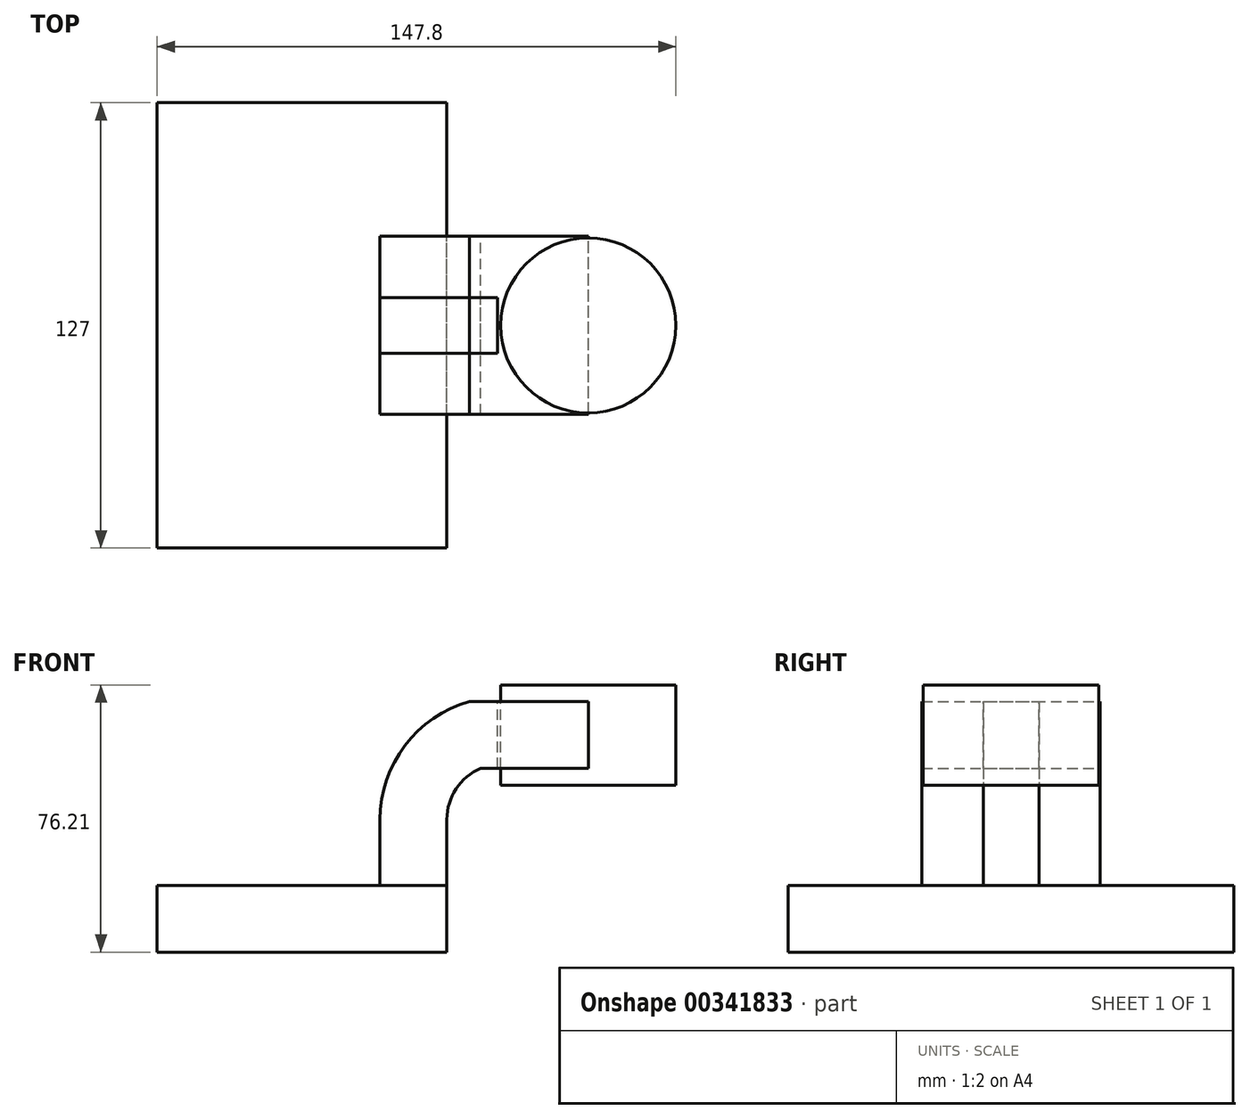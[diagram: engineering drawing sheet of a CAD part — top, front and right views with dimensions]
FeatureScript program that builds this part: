
annotation { "Feature Type Name" : "Feature", "Feature Type Description" : "" }
export const myFeature = defineFeature(function(context is Context, id is Id, definition is map)
    precondition{}
    {
        {
            var Q0;
            Q0=qCreatedBy(makeId("Front.planeOp"),FACE);
            var sketch = newSketch(context, id + "F0", { "sketchPlane" : qUnion([Q0])});
            skLineSegment(sketch, "E0.bottom", {"start": v(41.28, -9.52) * mm, "end": v(-41.28, -9.53) * mm});
            skLineSegment(sketch, "E0.top", {"start": v(41.28, 9.53) * mm, "end": v(-41.28, 9.53) * mm});
            skLineSegment(sketch, "E0.left", {"start": v(41.28, -9.52) * mm, "end": v(41.28, 9.53) * mm});
            skLineSegment(sketch, "E0.right", {"start": v(-41.28, -9.53) * mm, "end": v(-41.28, 9.53) * mm});
            skPoint(sketch, "E0.middle", {"position": v(0, 0) * mm});
            skLineSegment(sketch, "E1.bottom", {"start": v(106.53, 38.1) * mm, "end": v(55.73, 38.1) * mm});
            skLineSegment(sketch, "E1.top", {"start": v(106.53, 66.68) * mm, "end": v(55.73, 66.68) * mm});
            skLineSegment(sketch, "E1.left", {"start": v(106.53, 38.1) * mm, "end": v(106.53, 66.68) * mm});
            skLineSegment(sketch, "E1.right", {"start": v(55.73, 38.1) * mm, "end": v(55.73, 66.68) * mm});
            skPoint(sketch, "E1.middle", {"position": v(81.13, 52.39) * mm});
            skLineSegment(sketch, "E2", {"start": v(41.28, 9.53) * mm, "end": v(41.28, 28.3) * mm});
            skArc(sketch, "E3", {"start": v(41.27, 28.3) * mm, "mid": v(43.9, 37.02) * mm, "end": v(50.88, 42.88) * mm});
            skLineSegment(sketch, "E4", {"start": v(50.88, 42.88) * mm, "end": v(81.56, 42.88) * mm});
            skLineSegment(sketch, "E5.0", {"start": v(47.74, 61.93) * mm, "end": v(81.56, 61.93) * mm});
            skArc(sketch, "E5.1", {"start": v(22.22, 28.3) * mm, "mid": v(29.33, 49.4) * mm, "end": v(47.74, 61.93) * mm});
            skLineSegment(sketch, "E5.2", {"start": v(22.22, 9.53) * mm, "end": v(22.22, 28.3) * mm});
            skFitSpline(sketch, "E6", {"points": [v(-41.28, 9.53) * mm, v(47.74, 61.93) * mm], "startDerivative": vector(-2.2, 95.89) * mm, "endDerivative": vector(156.54, 0.26) * mm});
            skLineSegment(sketch, "E7", {"start": v(81.56, 42.88) * mm, "end": v(81.56, 61.93) * mm});
            skLineSegment(sketch, "E8", {"start": v(81.56, 66.68) * mm, "end": v(81.56, 38.1) * mm});
            skSolve(sketch);
        }
        {
            var Q0;
            Q0=makeQuery(id+"F0.imprint","IMPRINT",FACE,{"disambiguationData":[TD([[makeQuery(id+"F0.imprint","IMPRINT",EDGE,{"derivedFrom":sQuery(id+"F0.wireOp",EDGE,"E0.bottom")}),-1.0]])]});
            extrude(context, id + "F1", {"entities" : qUnion([Q0]), "endBound" : BoundingType.SYMMETRIC, "depth" : 127 * mm});
        }
        {
            var Q0;
            {var subQ0=sQuery(id+"F0.wireOp",EDGE,"E4");var subQ1=sQuery(id+"F0.wireOp",EDGE,"E1.right");var subQ2=makeQuery(id+"F0.imprint","INTERSECT",VERTEX,{"derivedFrom":[subQ1,subQ0]});Q0=makeQuery(id+"F0.imprint","IMPRINT",FACE,{"disambiguationData":[TD([[makeQuery(id+"F0.imprint","IMPRINT",EDGE,{"disambiguationData":[TD([[subQ2,-1.0]])],"derivedFrom":subQ1}),-1.0]])]});}
            var Q1;
            {var subQ1=sQuery(id+"F0.wireOp",EDGE,"E2");Q1=makeQuery(id+"F0.imprint","IMPRINT",FACE,{"disambiguationData":[TD([[makeQuery(id+"F0.imprint","IMPRINT",EDGE,{"derivedFrom":subQ1}),1.0]])]});}
            extrude(context, id + "F2", {"entities" : qUnion([Q0, Q1]), "endBound" : BoundingType.SYMMETRIC, "depth" : 50.8 * mm});
        }
        {
            var Q0;
            Q0=makeQuery(id+"F0.imprint","IMPRINT",FACE,{"disambiguationData":[TD([[makeQuery(id+"F0.imprint","IMPRINT",EDGE,{"derivedFrom":sQuery(id+"F0.wireOp",EDGE,"E5.1")}),1.0]])]});
            extrude(context, id + "F3", {"entities" : qUnion([Q0]), "endBound" : BoundingType.SYMMETRIC, "depth" : 15.88 * mm});
        }
        {
            var Q0;
            {var subQ0=sQuery(id+"F0.wireOp",EDGE,"E1.left");Q0=makeQuery(id+"F0.imprint","IMPRINT",FACE,{"disambiguationData":[TD([[makeQuery(id+"F0.imprint","IMPRINT",EDGE,{"derivedFrom":subQ0}),1.0]])]});}
            var Q1;
            Q1=sQuery(id+"F0.wireOp",EDGE,"E8");
            revolve(context, id + "F4", {"entities" : qUnion([Q0]), "axis" : qUnion([Q1]), "revolveType" : RevolveType.FULL});
        }
    });
